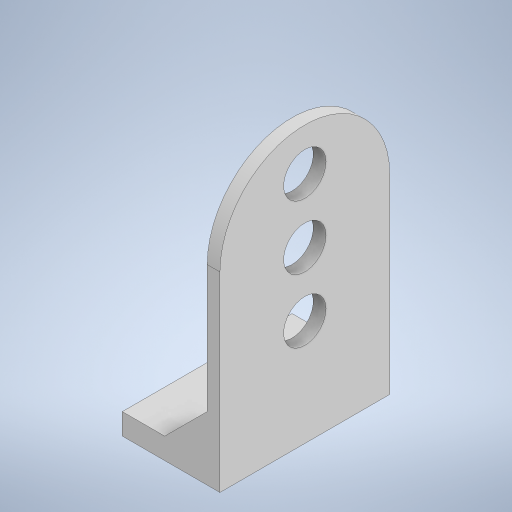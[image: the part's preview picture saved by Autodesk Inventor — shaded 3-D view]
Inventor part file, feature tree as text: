
AUTODESK INVENTOR PART (.ipt)
format: ipt  version: 2023 (Build 270158000, 158)  size: 253,440 bytes
history: native  units: mm
features: extrude x3, sketch x3, chamfer x1, fillet x1
ambient origin geometry x8: Origin, YZ Plane, XZ Plane, XY Plane, X Axis, Y Axis, Z Axis, Center Point
bodies: Solid1 (feature_tree)
feature tree (8):
  extrude  "Extrusion1"  Depth=65.0mm
  extrude  "Extrusion2"  Depth=5.0mm
  chamfer  "Chamfer1"  Distance=20.0mm
  extrude  "Extrusion3"  Depth=10.0mm
  fillet  "Fillet1"  Radius=10.0mm
  sketch  "Sketch1"  dims[d0=40.0mm d1=65.0mm]
  sketch  "Sketch2"  dims[d2=3.0mm d3=0.0mm d4=5.0mm d5=20.0mm d6=0.0mm]
  sketch  "Sketch3"  dims[d7=10.0mm d8=2.0mm d9=45.0deg d10=10.0mm d11=10.0mm d12=5.0mm d13=15.0mm d14=20.0mm d15=0.0mm d16=0.0mm d17=20.0mm]
